FCSTD DOCUMENT  (FreeCAD 0.20R29177 +426 (Git))
Label: ASM_ExtensionArm
License: All rights reserved
LicenseURL: http://en.wikipedia.org/wiki/All_rights_reserved
objects: App::Link×7, App::DocumentObjectGroup×4, PartDesign::CoordinateSystem×3, App::FeaturePython×1, Part::FeaturePython×1, App::Part×1
note: 4 computed .brp shape members not serialized (recipe doc carries the construction recipe); baked Part::Feature solids carry a one-line shape summary decoded from their .brp
EXTERNAL_REF file=ASM_GantrySkate.FCStd obj=LCS_Origin
EXTERNAL_REF file=Params.FCStd obj=Spreadsheet
EXTERNAL_REF file=ASM_GantrySkate.FCStd obj=Assembly
EXTERNAL_REF file=../../../../../../AppData/Local/Temp/FreeCAD/Cache/FreeCAD_Doc_665ddbc1-c403-4c85-9c79-733a05948db3_da39a3_5468 obj=Assembly
EXTERNAL_REF file=AlExtrusion2040.FCStd obj=Assembly
EXTERNAL_REF file=ASM_ExtensionDriver.FCStd obj=LCS_Origin
EXTERNAL_REF file=ASM_ExtensionDriver.FCStd obj=Assembly
EXTERNAL_REF file=EndStopRear.FCStd obj=LCS_Origin
EXTERNAL_REF file=EndStopRear.FCStd obj=Assembly
EXTERNAL_REF file=BeltRetainerRear.FCStd obj=LCS_Origin
EXTERNAL_REF file=BeltRetainerRear.FCStd obj=Assembly
EXTERNAL_REF file=ASM_ExtensionHead.FCStd obj=LCS_Origin
EXTERNAL_REF file=ASM_ExtensionHead.FCStd obj=Assembly

FEATURE [App::DocumentObjectGroup] Parts
FEATURE [PartDesign::CoordinateSystem] LCS_Origin
  AttacherType = Attacher::AttachEngine3D
  MapMode = 2
  Support = -> [X_Axis]
FEATURE [App::FeaturePython] Variables  # WARN: FeaturePython — macro-defined, semantics opaque (R4)
  Retraction = 300
  Type = App::PropertyContainer
FEATURE [App::DocumentObjectGroup] Constraints
FEATURE [App::DocumentObjectGroup] Configurations
FEATURE [App::Link] ASM_GantrySkate  label="ASM_GantrySkate001"
  AttachedBy = #LCS_Origin
  AttachedTo = Parent Assembly#LCS_Origin
  AttachmentOffset = pos=(0,-150,0) rot=(0,1,0;3.14159rad)
  LinkPlacement = pos=(0,-150,0) rot=(0,1,0;3.14159rad)
  LinkedObject = -> <external ASM_GantrySkate.FCStd>#Assembly
  Placement = pos=(0,-150,0) rot=(0,1,0;3.14159rad)
  SolverId = Asm4EE
  expr: .AttachmentOffset.Base.y = <<Params>>#<<Params>>.RearSkateOffset * -1
  expr: Placement = LCS_Origin.Placement * AttachmentOffset * ASM_GantrySkate#LCS_Origin.Placement ^ -1
FEATURE [App::Link] ASM_GantrySkate001  label="ASM_GantrySkate002"
  AttachedBy = #LCS_Origin
  AttachedTo = Parent Assembly#LCS_Origin
  AttachmentOffset = pos=(0,350,0) rot=(0,1,0;3.14159rad)
  LinkPlacement = pos=(0,350,0) rot=(0,1,0;3.14159rad)
  LinkedObject = -> <external ASM_GantrySkate.FCStd>#Assembly
  Placement = pos=(0,350,0) rot=(0,1,0;3.14159rad)
  SolverId = Asm4EE
  expr: .AttachmentOffset.Base.y = <<Params>>#<<Params>>.FrontSkateOffset
  expr: Placement = LCS_Origin.Placement * AttachmentOffset * ASM_GantrySkate#LCS_Origin.Placement ^ -1
FEATURE [Part::FeaturePython] AlExtrusion2040_var  # link proxy (typed FeaturePython)
  AttachedBy = #LCS_Origin
  AttachedTo = Parent Assembly#LCS_EndStop
  AttachmentOffset = pos=(0,0,0) rot=(0.57735,-0.57735,-0.57735;4.18879rad)
  Length = 2000
  LinkedObject = -> <external ../../../../../../AppData/Local/Temp/FreeCAD/Cache/FreeCAD_Doc_665ddbc1-c403-4c85-9c79-733a05948db3_da39a3_5468>#Assembly
  Placement = pos=(2.9e-15,-482,-23.5) rot=(-0.57735,-0.57735,-0.57735;2.0944rad)
  SolverId = Asm4EE
  SourceObject = -> <external AlExtrusion2040.FCStd>#Assembly
  expr: Placement = LCS_EndStop.Placement * AttachmentOffset * varTmpDoc_3#LCS_Origin.Placement ^ -1
FEATURE [App::Link] ASM_ExtensionDriver
  AttachedBy = #LCS_Origin
  AttachedTo = Parent Assembly#LCS_Origin
  AttachmentOffset = pos=(-36,100,0) rot=(0.707107,0.707107,0;3.14159rad)
  LinkPlacement = pos=(-36,100,0) rot=(0.707107,0.707107,0;3.14159rad)
  LinkedObject = -> <external ASM_ExtensionDriver.FCStd>#Assembly
  Placement = pos=(-36,100,0) rot=(0.707107,0.707107,0;3.14159rad)
  SolverId = Asm4EE
  expr: Placement = LCS_Origin.Placement * AttachmentOffset * ASM_ExtensionDriver#LCS_Origin.Placement ^ -1
FEATURE [App::DocumentObjectGroup] Fasteners
FEATURE [App::Link] EndStopRear
  AttachedBy = #LCS_Origin
  AttachedTo = Parent Assembly#LCS_EndStop
  AttachmentOffset = pos=(0,0,0) rot=(1,0,0;1.5708rad)
  LinkPlacement = pos=(2.9e-15,-482,-23.5) rot=(0,0.707107,-0.707107;3.14159rad)
  LinkedObject = -> <external EndStopRear.FCStd>#Assembly
  Placement = pos=(2.9e-15,-482,-23.5) rot=(0,0.707107,-0.707107;3.14159rad)
  SolverId = Asm4EE
  expr: Placement = LCS_EndStop.Placement * AttachmentOffset * EndStopRear#LCS_Origin.Placement ^ -1
FEATURE [PartDesign::CoordinateSystem] ASM_GantrySkate_LCS_Origin
  AttachedBy = Origin
  AttacherType = Attacher::AttachEngine3D
  Placement = pos=(0,-150,0) rot=(0,1,0;3.14159rad)
  SolverId = Asm4EE
  expr: Placement = ASM_GantrySkate.Placement * ASM_GantrySkate#LCS_Origin.Placement
FEATURE [PartDesign::CoordinateSystem] LCS_EndStop
  AttacherType = Attacher::AttachEngine3D
  AttachmentOffset = pos=(0,-332,23.5) rot=(0,0,1;0rad)
  MapMode = 2
  Placement = pos=(2.9e-15,-482,-23.5) rot=(0,1,0;3.14159rad)
  Support = -> [ASM_GantrySkate_LCS_Origin]
  expr: .AttachmentOffset.Base.y = -32 - <<Variables>>.Retraction
FEATURE [App::Link] BeltRetainerRear
  AttachedBy = #LCS_Origin
  AttachedTo = Parent Assembly#LCS_EndStop
  AttachmentOffset = pos=(10,30,10) rot=(0.57735,0.57735,0.57735;2.0944rad)
  LinkPlacement = pos=(-10,-452,-33.5) rot=(0.57735,0.57735,-0.57735;4.18879rad)
  LinkedObject = -> <external BeltRetainerRear.FCStd>#Assembly
  Placement = pos=(-10,-452,-33.5) rot=(0.57735,0.57735,-0.57735;4.18879rad)
  SolverId = Asm4EE
  expr: Placement = LCS_EndStop.Placement * AttachmentOffset * BeltRetainerRear#LCS_Origin.Placement ^ -1
FEATURE [App::Link] BeltRetainerRear001  label="BeltRetainerTip"
  AttachedBy = #LCS_Origin
  AttachedTo = Parent Assembly#LCS_EndStop
  AttachmentOffset = pos=(10,1977,10) rot=(0.57735,-0.57735,0.57735;4.18879rad)
  LinkPlacement = pos=(-10,1495,-33.5) rot=(0.57735,-0.57735,-0.57735;2.0944rad)
  LinkedObject = -> <external BeltRetainerRear.FCStd>#Assembly
  Placement = pos=(-10,1495,-33.5) rot=(0.57735,-0.57735,-0.57735;2.0944rad)
  SolverId = Asm4EE
  expr: Placement = LCS_EndStop.Placement * AttachmentOffset * BeltRetainerRear#LCS_Origin.Placement ^ -1
FEATURE [App::Link] ASM_ExtensionHead
  AttachedBy = #LCS_Origin
  AttachedTo = Parent Assembly#LCS_EndStop
  AttachmentOffset = pos=(0,2000,0) rot=(0,1,0;3.14159rad)
  LinkPlacement = pos=(2.9e-15,1518,-23.5) rot=(0,0,1;0rad)
  LinkedObject = -> <external ASM_ExtensionHead.FCStd>#Assembly
  Placement = pos=(2.9e-15,1518,-23.5) rot=(0,0,1;0rad)
  SolverId = Asm4EE
  expr: .AttachmentOffset.Base.y = <<AlExtrusion2040_var>>.Length
  expr: Placement = LCS_EndStop.Placement * AttachmentOffset * ASM_ExtensionHead#LCS_Origin.Placement ^ -1
FEATURE [App::Part] Assembly
  AssemblyType = Part::Link
  Group = -> [LCS_Origin,Variables,Constraints,Configurations,ASM_GantrySkate,ASM_GantrySkate001,AlExtrusion2040_var,ASM_ExtensionDriver,Fasteners,EndStopRear,LCS_EndStop,ASM_GantrySkate_LCS_Origin,BeltRetainerRear,BeltRetainerRear001,ASM_ExtensionHead]
  Origin = -> Origin
  Type = Assembly

RESOLVED EXTERNAL PARTS (link-assembly join: the EXTERNAL_REF files above that resolve inside this repo's crawl, each included once):
---- part ASM_ExtensionDriver.FCStd = doc fcstd_9ed249eb061f ----
FCSTD DOCUMENT  (FreeCAD 0.20R29177 +426 (Git))
Label: ASM_ExtensionDriver
License: All rights reserved
LicenseURL: http://en.wikipedia.org/wiki/All_rights_reserved
objects: App::Link×5, App::DocumentObjectGroup×3, PartDesign::CoordinateSystem×1, App::FeaturePython×1, App::Part×1
note: 1 computed .brp shape members not serialized (recipe doc carries the construction recipe); baked Part::Feature solids carry a one-line shape summary decoded from their .brp
EXTERNAL_REF file=ASM_Stepper.FCStd obj=LCS_Origin
EXTERNAL_REF file=ASM_Stepper.FCStd obj=Assembly
EXTERNAL_REF file=ASM_Stepper.FCStd obj=Stepper_LCS_mount
EXTERNAL_REF file=SerpentinePlate.FCStd obj=LCS_Origin
EXTERNAL_REF file=SerpentinePlate.FCStd obj=Assembly
EXTERNAL_REF file=TimingPulleyGT2.FCStd obj=LCS_Origin
EXTERNAL_REF file=TimingPulleyGT2.FCStd obj=Assembly
EXTERNAL_REF file=SerpentinePlate.FCStd obj=LCS_idler1
EXTERNAL_REF file=SmoothIdlerPulleyGT2.FCStd obj=LCS_Origin
EXTERNAL_REF file=SmoothIdlerPulleyGT2.FCStd obj=Assembly
EXTERNAL_REF file=SerpentinePlate.FCStd obj=LCS_idler2

FEATURE [App::DocumentObjectGroup] Parts
FEATURE [PartDesign::CoordinateSystem] LCS_Origin
  AttacherType = Attacher::AttachEngine3D
  MapMode = 2
  Support = -> [X_Axis]
FEATURE [App::FeaturePython] Variables  # WARN: FeaturePython — macro-defined, semantics opaque (R4)
  Type = App::PropertyContainer
FEATURE [App::DocumentObjectGroup] Constraints
FEATURE [App::DocumentObjectGroup] Configurations
FEATURE [App::Link] ASM_Stepper
  AttachedBy = #LCS_Origin
  AttachedTo = Parent Assembly#LCS_Origin
  LinkedObject = -> <external ASM_Stepper.FCStd>#Assembly
  SolverId = Asm4EE
  expr: Placement = LCS_Origin.Placement * AttachmentOffset * ASM_Stepper#LCS_Origin.Placement ^ -1
FEATURE [App::Link] SerpentinePlate
  AttachedBy = #LCS_Origin
  AttachedTo = ASM_Stepper#Stepper_LCS_mount
  AttachmentOffset = pos=(0,0,-3) rot=(-1,0,0;3.14159rad)
  LinkPlacement = pos=(0,-7.1e-15,30) rot=(-1,0,0;1.5708rad)
  LinkedObject = -> <external SerpentinePlate.FCStd>#Assembly
  Placement = pos=(0,-7.1e-15,30) rot=(-1,0,0;1.5708rad)
  SolverId = Asm4EE
  expr: Placement = ASM_Stepper.Placement * ASM_Stepper#Stepper_LCS_mount.Placement * AttachmentOffset * SerpentinePlate#LCS_Origin.Placement ^ -1
FEATURE [App::Link] TimingPulleyGT2
  AttachedBy = #LCS_Origin
  AttachedTo = ASM_Stepper#Stepper_LCS_mount
  AttachmentOffset = pos=(0,0,-26) rot=(0,0,1;0rad)
  LinkPlacement = pos=(0,23,30) rot=(1,0,0;1.5708rad)
  LinkedObject = -> <external TimingPulleyGT2.FCStd>#Assembly
  Placement = pos=(0,23,30) rot=(1,0,0;1.5708rad)
  SolverId = Asm4EE
  expr: Placement = ASM_Stepper.Placement * ASM_Stepper#Stepper_LCS_mount.Placement * AttachmentOffset * TimingPulleyGT2#LCS_Origin.Placement ^ -1
FEATURE [App::Link] SmoothIdlerPulleyGT2
  AttachedBy = #LCS_Origin
  AttachedTo = SerpentinePlate#LCS_idler1
  AttachmentOffset = pos=(0,0,1) rot=(0,0,1;0rad)
  LinkPlacement = pos=(16.3,8,37.5) rot=(-1,0,0;1.5708rad)
  LinkedObject = -> <external SmoothIdlerPulleyGT2.FCStd>#Assembly
  Placement = pos=(16.3,8,37.5) rot=(-1,0,0;1.5708rad)
  SolverId = Asm4EE
  expr: Placement = SerpentinePlate.Placement * SerpentinePlate#LCS_idler1.Placement * AttachmentOffset * SmoothIdlerPulleyGT2#LCS_Origin.Placement ^ -1
FEATURE [App::Link] SmoothIdlerPulleyGT003
  AttachedBy = #LCS_Origin
  AttachedTo = SerpentinePlate#LCS_idler2
  AttachmentOffset = pos=(0,0,1) rot=(0,0,1;0rad)
  LinkPlacement = pos=(-16.3,8,37.5) rot=(-1,0,0;1.5708rad)
  LinkedObject = -> <external SmoothIdlerPulleyGT2.FCStd>#Assembly
  Placement = pos=(-16.3,8,37.5) rot=(-1,0,0;1.5708rad)
  SolverId = Asm4EE
  expr: Placement = SerpentinePlate.Placement * SerpentinePlate#LCS_idler2.Placement * AttachmentOffset * SmoothIdlerPulleyGT2#LCS_Origin.Placement ^ -1
FEATURE [App::Part] Assembly
  AssemblyType = Part::Link
  Group = -> [LCS_Origin,Variables,Constraints,Configurations,ASM_Stepper,SerpentinePlate,TimingPulleyGT2,SmoothIdlerPulleyGT2,SmoothIdlerPulleyGT003]
  Origin = -> Origin
  Type = Assembly
---- part ASM_ExtensionHead.FCStd = doc fcstd_2c640205720b ----
FCSTD DOCUMENT  (FreeCAD 0.20R29177 +426 (Git))
Label: ASM_ExtensionHead
License: All rights reserved
LicenseURL: http://en.wikipedia.org/wiki/All_rights_reserved
objects: App::Link×6, App::DocumentObjectGroup×3, PartDesign::CoordinateSystem×1, App::FeaturePython×1, App::Part×1
note: 1 computed .brp shape members not serialized (recipe doc carries the construction recipe); baked Part::Feature solids carry a one-line shape summary decoded from their .brp
EXTERNAL_REF file=EndStopTip.FCStd obj=LCS_Origin
EXTERNAL_REF file=EndStopTip.FCStd obj=Assembly
EXTERNAL_REF file=BreakawayMagnet.FCStd obj=LCS_Origin
EXTERNAL_REF file=EndStopTip.FCStd obj=Variables
EXTERNAL_REF file=BreakawayMagnet.FCStd obj=Assembly
EXTERNAL_REF file=BreakawayHeadBase.FCStd obj=LCS_Origin
EXTERNAL_REF file=EndStopTip.FCStd obj=Pad
EXTERNAL_REF file=EndStopTip.FCStd obj=Pad001
EXTERNAL_REF file=BreakawayHeadBase.FCStd obj=Assembly
EXTERNAL_REF file=ASM_TrussPulley.FCStd obj=LCS_Origin
EXTERNAL_REF file=BreakawayHeadBase.FCStd obj=Sketch002
EXTERNAL_REF file=BreakawayHeadTruss.FCStd obj=Variables
EXTERNAL_REF file=ASM_TrussPulley.FCStd obj=Assembly
EXTERNAL_REF file=HeadTetherMountClip.FCStd obj=LCS_Origin
EXTERNAL_REF file=HeadTetherMountClip.FCStd obj=Assembly

FEATURE [App::DocumentObjectGroup] Parts
FEATURE [PartDesign::CoordinateSystem] LCS_Origin
  AttacherType = Attacher::AttachEngine3D
  MapMode = 2
  Support = -> [X_Axis]
FEATURE [App::FeaturePython] Variables  # WARN: FeaturePython — macro-defined, semantics opaque (R4)
  Type = App::PropertyContainer
FEATURE [App::DocumentObjectGroup] Constraints
FEATURE [App::DocumentObjectGroup] Configurations
FEATURE [App::Link] EndStopTip
  AttachedBy = #LCS_Origin
  AttachedTo = Parent Assembly#LCS_Origin
  AttachmentOffset = pos=(0,0,0) rot=(0,-0.707107,-0.707107;3.14159rad)
  LinkPlacement = pos=(0,0,0) rot=(0,-0.707107,-0.707107;3.14159rad)
  LinkedObject = -> <external EndStopTip.FCStd>#Assembly
  Placement = pos=(0,0,0) rot=(0,-0.707107,-0.707107;3.14159rad)
  SolverId = Asm4EE
  expr: Placement = LCS_Origin.Placement * AttachmentOffset * EndStopTip#LCS_Origin.Placement ^ -1
FEATURE [App::Link] BreakawayMagnet  label="BreakawayMagnetTop"
  AttachedBy = #LCS_Origin
  AttachedTo = EndStopTip#LCS_Origin
  AttachmentOffset = pos=(0,-10,5) rot=(0,0,1;0rad)
  LinkPlacement = pos=(-1.3e-15,5,-10) rot=(0,-0.707107,-0.707107;3.14159rad)
  LinkedObject = -> <external BreakawayMagnet.FCStd>#Assembly
  Placement = pos=(-1.3e-15,5,-10) rot=(0,-0.707107,-0.707107;3.14159rad)
  SolverId = Asm4EE
  expr: .AttachmentOffset.Base.z = <<EndStopTip>>#<<Variables>>.BaseHeight
  expr: Placement = EndStopTip.Placement * EndStopTip#LCS_Origin.Placement * AttachmentOffset * BreakawayMagnet#LCS_Origin.Placement ^ -1
FEATURE [App::Link] BreakawayMagnet001  label="BreakawayMagnetBottom"
  AttachedBy = #LCS_Origin
  AttachedTo = EndStopTip#LCS_Origin
  AttachmentOffset = pos=(0,10,5) rot=(0,0,1;0rad)
  LinkPlacement = pos=(4e-16,5,10) rot=(0,-0.707107,-0.707107;3.14159rad)
  LinkedObject = -> <external BreakawayMagnet.FCStd>#Assembly
  Placement = pos=(4e-16,5,10) rot=(0,-0.707107,-0.707107;3.14159rad)
  SolverId = Asm4EE
  expr: .AttachmentOffset.Base.z = <<EndStopTip>>#<<Variables>>.BaseHeight
  expr: Placement = EndStopTip.Placement * EndStopTip#LCS_Origin.Placement * AttachmentOffset * BreakawayMagnet#LCS_Origin.Placement ^ -1
FEATURE [App::Link] BreakawayHeadBase
  AttachedBy = #LCS_Origin
  AttachedTo = EndStopTip#LCS_Origin
  AttachmentOffset = pos=(0,0,10) rot=(0,-0.707107,0.707107;3.14159rad)
  LinkPlacement = pos=(-9e-16,10,-2.2e-15) rot=(-1,0,0;3.14159rad)
  LinkedObject = -> <external BreakawayHeadBase.FCStd>#Assembly
  Placement = pos=(-9e-16,10,-2.2e-15) rot=(-1,0,0;3.14159rad)
  SolverId = Asm4EE
  expr: .AttachmentOffset.Base.z = <<EndStopTip>>#<<Pad>>.Length + <<EndStopTip>>#<<MagnetPad>>.Length
  expr: Placement = EndStopTip.Placement * EndStopTip#LCS_Origin.Placement * AttachmentOffset * BreakawayHeadBase#LCS_Origin.Placement ^ -1
FEATURE [App::Link] ASM_TrussPulley
  AttachedBy = #LCS_Origin
  AttachedTo = BreakawayHeadBase#LCS_Origin
  AttachmentOffset = pos=(0,-18,-16) rot=(1,0,0;3.40339rad)
  LinkPlacement = pos=(-4e-15,28,16) rot=(1,0,0;0.261799rad)
  LinkedObject = -> <external ASM_TrussPulley.FCStd>#Assembly
  Placement = pos=(-4e-15,28,16) rot=(1,0,0;0.261799rad)
  SolverId = Asm4EE
  expr: .AttachmentOffset.Base.y = <<BreakawayHeadBase>>#<<Sketch002>>.Constraints.HolesOffset * -1
  expr: .AttachmentOffset.Base.z = <<BreakawayHeadBase>>#<<Sketch002>>.Constraints.TrussHoleSpacing / -2
  expr: .AttachmentOffset.Rotation.Angle = 180 + <<BreakawayHeadTruss>>#<<Variables>>.TrussAngle
  expr: Placement = BreakawayHeadBase.Placement * BreakawayHeadBase#LCS_Origin.Placement * AttachmentOffset * ASM_TrussPulley#LCS_Origin.Placement ^ -1
FEATURE [App::Link] HeadTetherMountClip
  AttachedBy = #LCS_Origin
  AttachedTo = Parent Assembly#LCS_Origin
  AttachmentOffset = pos=(10,-18,-10) rot=(0.57735,0.57735,0.57735;2.0944rad)
  LinkPlacement = pos=(10,-18,-10) rot=(0.57735,0.57735,0.57735;2.0944rad)
  LinkedObject = -> <external HeadTetherMountClip.FCStd>#Assembly
  Placement = pos=(10,-18,-10) rot=(0.57735,0.57735,0.57735;2.0944rad)
  SolverId = Asm4EE
  expr: Placement = LCS_Origin.Placement * AttachmentOffset * HeadTetherMountClip#LCS_Origin.Placement ^ -1
FEATURE [App::Part] Assembly
  AssemblyType = Part::Link
  Group = -> [LCS_Origin,Variables,Constraints,Configurations,EndStopTip,BreakawayMagnet,BreakawayMagnet001,BreakawayHeadBase,ASM_TrussPulley,HeadTetherMountClip]
  Origin = -> Origin
  Type = Assembly
---- part ASM_GantrySkate.FCStd = doc fcstd_b04221d5cb82 ----
FCSTD DOCUMENT  (FreeCAD 0.20R29177 +426 (Git))
Label: ASM_GantrySkate
License: All rights reserved
LicenseURL: http://en.wikipedia.org/wiki/All_rights_reserved
objects: Part::FeaturePython×6, App::Link×5, App::DocumentObjectGroup×4, PartDesign::CoordinateSystem×1, App::FeaturePython×1, App::Part×1
note: 7 computed .brp shape members not serialized (recipe doc carries the construction recipe); baked Part::Feature solids carry a one-line shape summary decoded from their .brp
EXTERNAL_REF file=GantryBracket.FCStd obj=LCS_Origin
EXTERNAL_REF file=GantryBracket.FCStd obj=Assembly
EXTERNAL_REF file=GantryBracket.FCStd obj=LCS_wheel1
EXTERNAL_REF file=GantryWheel.FCStd obj=LCS_Origin
EXTERNAL_REF file=GantryWheel.FCStd obj=Assembly
EXTERNAL_REF file=GantryBracket.FCStd obj=LCS_wheel2
EXTERNAL_REF file=GantryBracket.FCStd obj=LCS_wheel3
EXTERNAL_REF file=GantryBracket.FCStd obj=LCS_wheel4
EXTERNAL_REF file=Params.FCStd obj=Spreadsheet
EXTERNAL_REF file=GantryBracket.FCStd obj=Sketch
EXTERNAL_REF file=GantryBracket.FCStd obj=Pad

FEATURE [App::DocumentObjectGroup] Parts
FEATURE [PartDesign::CoordinateSystem] LCS_Origin
  AttacherType = Attacher::AttachEngine3D
  MapMode = 2
  Support = -> [X_Axis]
FEATURE [App::FeaturePython] Variables  # WARN: FeaturePython — macro-defined, semantics opaque (R4)
  Type = App::PropertyContainer
FEATURE [App::DocumentObjectGroup] Constraints
FEATURE [App::DocumentObjectGroup] Configurations
FEATURE [App::Link] GantryBracket
  AttachedBy = #LCS_Origin
  AttachedTo = Parent Assembly#LCS_Origin
  LinkedObject = -> <external GantryBracket.FCStd>#Assembly
  SolverId = Asm4EE
  expr: Placement = LCS_Origin.Placement * AttachmentOffset * GantryBracket#LCS_Origin.Placement ^ -1
FEATURE [App::Link] GantryWheel
  AttachedBy = #LCS_Origin
  AttachedTo = GantryBracket#LCS_wheel1
  LinkPlacement = pos=(-19.85,20,3) rot=(0,0,1;1.5708rad)
  LinkedObject = -> <external GantryWheel.FCStd>#Assembly
  Placement = pos=(-19.85,20,3) rot=(0,0,1;1.5708rad)
  SolverId = Asm4EE
  expr: Placement = GantryBracket.Placement * GantryBracket#LCS_wheel1.Placement * AttachmentOffset * GantryWheel#LCS_Origin.Placement ^ -1
FEATURE [App::Link] GantryWheel001
  AttachedBy = #LCS_Origin
  AttachedTo = GantryBracket#LCS_wheel2
  LinkPlacement = pos=(19.85,20,3) rot=(0,0,1;1.5708rad)
  LinkedObject = -> <external GantryWheel.FCStd>#Assembly
  Placement = pos=(19.85,20,3) rot=(0,0,1;1.5708rad)
  SolverId = Asm4EE
  expr: Placement = GantryBracket.Placement * GantryBracket#LCS_wheel2.Placement * AttachmentOffset * GantryWheel#LCS_Origin.Placement ^ -1
FEATURE [App::Link] GantryWheel002
  AttachedBy = #LCS_Origin
  AttachedTo = GantryBracket#LCS_wheel3
  LinkPlacement = pos=(-19.85,-20,3) rot=(0,0,1;1.5708rad)
  LinkedObject = -> <external GantryWheel.FCStd>#Assembly
  Placement = pos=(-19.85,-20,3) rot=(0,0,1;1.5708rad)
  SolverId = Asm4EE
  expr: Placement = GantryBracket.Placement * GantryBracket#LCS_wheel3.Placement * AttachmentOffset * GantryWheel#LCS_Origin.Placement ^ -1
FEATURE [App::Link] GantryWheel003
  AttachedBy = #LCS_Origin
  AttachedTo = GantryBracket#LCS_wheel4
  LinkPlacement = pos=(19.85,-20,3) rot=(0,0,1;1.5708rad)
  LinkedObject = -> <external GantryWheel.FCStd>#Assembly
  Placement = pos=(19.85,-20,3) rot=(0,0,1;1.5708rad)
  SolverId = Asm4EE
  expr: Placement = GantryBracket.Placement * GantryBracket#LCS_wheel4.Placement * AttachmentOffset * GantryWheel#LCS_Origin.Placement ^ -1
FEATURE [Part::FeaturePython] Screw  label="M5x16-Screw"  # Fasteners workbench fastener (typed FeaturePython)
  Placement = pos=(19.85,0,-3.156) rot=(1,0,0;3.14159rad)
  baseObject = -> <external GantryBracket.FCStd>#Sketch [Edge23]
  diameter = 5
  invert = true
  leftHanded = false
  length = 3
  lengthCustom = 16
  matchOuter = false
  offset = 3.156
  thread = false
  type = 18
  expr: offset = <<Params>>#<<Params>>.SheetMetalThickness * 1mm + 0.5mm
FEATURE [Part::FeaturePython] Washer  label="M5-Washer"  # Fasteners workbench fastener (typed FeaturePython)
  Placement = pos=(19.85,0,3) rot=(0,0,1;0rad)
  baseObject = -> <external GantryBracket.FCStd>#Sketch [Edge23]
  diameter = 6
  invert = false
  matchOuter = false
  offset = 3
  type = 3
  expr: offset = <<GantryBracket>>#<<Pad>>.Length
FEATURE [Part::FeaturePython] Nut  label="M5-Nut"  # Fasteners workbench fastener (typed FeaturePython)
  Placement = pos=(19.85,0,4.1) rot=(0,0,1;0rad)
  baseObject = -> Washer [Edge1]
  diameter = 7
  invert = false
  leftHanded = false
  matchOuter = false
  offset = 0
  thread = false
  type = 7
FEATURE [Part::FeaturePython] Array_Screw  label="Array_M5x12-Screw"  # Draft array (typed FeaturePython)
  ArraySteps = 0
  ArrayType = Circular Array
  Axis = LCS_Origin.Z
  Count = 2
  ElementCount = 2
  FullAngle = 360
  IntervalAngle = 180
  LinearSteps = 0
  PlacementList = 2 placements: [(19.85,0,-3.156),(-19.85,2.43092e-15,-3.156)]
  ScaleList = (2) [(1,1,1),(1,1,1)]
  ShowElement = false
  SourceObject = -> Screw
FEATURE [Part::FeaturePython] Array_Washer  label="Array_M5-Washer"  # Draft array (typed FeaturePython)
  ArraySteps = 0
  ArrayType = Circular Array
  Axis = LCS_Origin.Z
  Count = 2
  ElementCount = 2
  FullAngle = 360
  IntervalAngle = 180
  LinearSteps = 0
  PlacementList = 2 placements: [(19.85,0,3),(-19.85,2.43092e-15,3)]
  ScaleList = (2) [(1,1,1),(1,1,1)]
  ShowElement = false
  SourceObject = -> Washer
FEATURE [Part::FeaturePython] Array_Nut  label="Array_M5-Nut"  # Draft array (typed FeaturePython)
  ArraySteps = 0
  ArrayType = Circular Array
  Axis = LCS_Origin.Z
  Count = 2
  ElementCount = 2
  FullAngle = 360
  IntervalAngle = 180
  LinearSteps = 0
  PlacementList = 2 placements: [(19.85,0,4.1),(-19.85,2.43092e-15,4.1)]
  ScaleList = (2) [(1,1,1),(1,1,1)]
  ShowElement = false
  SourceObject = -> Nut
FEATURE [App::DocumentObjectGroup] Fasteners
  Group = -> [Screw,Washer,Nut,Array_Screw,Array_Washer,Array_Nut]
FEATURE [App::Part] Assembly
  AssemblyType = Part::Link
  Group = -> [LCS_Origin,Variables,Constraints,Configurations,GantryBracket,GantryWheel,GantryWheel001,GantryWheel002,GantryWheel003,Fasteners,Screw,Array_Screw,Washer,Array_Washer,Nut,Array_Nut]
  Origin = -> Origin
  Type = Assembly
---- part AlExtrusion2040.FCStd = doc fcstd_94c1618523a2 ----
FCSTD DOCUMENT  (FreeCAD 0.20R29177 +426 (Git))
Label: AlExtrusion2040
License: All rights reserved
LicenseURL: http://en.wikipedia.org/wiki/All_rights_reserved
objects: App::DocumentObjectGroup×3, PartDesign::Mirrored×2, PartDesign::CoordinateSystem×1, App::FeaturePython×1, Sketcher::SketchObject×1, PartDesign::Pad×1, PartDesign::MultiTransform×1, PartDesign::Body×1, App::Part×1
note: 8 computed .brp shape members not serialized (recipe doc carries the construction recipe); baked Part::Feature solids carry a one-line shape summary decoded from their .brp

FEATURE [App::DocumentObjectGroup] Parts
FEATURE [PartDesign::CoordinateSystem] LCS_Origin
  AttacherType = Attacher::AttachEngine3D
  MapMode = 2
  Support = -> [X_Axis]
FEATURE [App::FeaturePython] Variables  # WARN: FeaturePython — macro-defined, semantics opaque (R4)
  Length = 100
  Type = App::PropertyContainer
FEATURE [App::DocumentObjectGroup] Constraints
FEATURE [App::DocumentObjectGroup] Configurations
FEATURE [Sketcher::SketchObject] Sketch
  FullyConstrained = true
  MapMode = 5
  Support = -> [XY_Plane001]
  sketch-geometry (30):
    g0: LineSegment StartX=0 StartY=10 StartZ=0 EndX=5.1 EndY=10 EndZ=0
    g1: LineSegment StartX=5.1 StartY=10 StartZ=0 EndX=6.9 EndY=8.2 EndZ=0
    g2: LineSegment StartX=6.9 StartY=8.2 StartZ=0 EndX=4.5 EndY=8.2 EndZ=0
    g3: LineSegment StartX=4.5 StartY=8.2 StartZ=0 EndX=4.5 EndY=6.56066 EndZ=0
    g4: LineSegment StartX=4.5 StartY=6.56066 StartZ=0 EndX=7.06066 EndY=4 EndZ=0
    g5: LineSegment StartX=7.06066 StartY=4 StartZ=0 EndX=12.9393 EndY=4 EndZ=0
    g6: LineSegment StartX=12.9393 StartY=4 StartZ=0 EndX=15.5 EndY=6.56066 EndZ=0
    g7: LineSegment StartX=15.5 StartY=6.56066 StartZ=0 EndX=15.5 EndY=8.2 EndZ=0
    g8: LineSegment StartX=15.5 StartY=8.2 StartZ=0 EndX=13.1 EndY=8.2 EndZ=0
    g9: LineSegment StartX=13.1 StartY=8.2 StartZ=0 EndX=14.9 EndY=10 EndZ=0
    g10: LineSegment StartX=14.9 StartY=10 StartZ=0 EndX=20 EndY=10 EndZ=0
    g11: LineSegment StartX=20 StartY=10 StartZ=0 EndX=20 EndY=4.9 EndZ=0
    g12: LineSegment StartX=20 StartY=4.9 StartZ=0 EndX=18.2 EndY=3.1 EndZ=0
    g13: LineSegment StartX=18.2 StartY=3.1 StartZ=0 EndX=18.2 EndY=5.5 EndZ=0
    g14: LineSegment StartX=18.2 StartY=5.5 StartZ=0 EndX=16.5607 EndY=5.5 EndZ=0
    g15: LineSegment StartX=16.5607 StartY=5.5 StartZ=0 EndX=14 EndY=2.93934 EndZ=0
    g16: LineSegment StartX=14 StartY=2.93934 StartZ=0 EndX=14 EndY=0 EndZ=0
    g17: LineSegment StartX=14 StartY=2.93934 StartZ=0 EndX=12.9393 EndY=4 EndZ=0
    g18: LineSegment StartX=14 StartY=0 StartZ=0 EndX=12.1 EndY=0 EndZ=0
    g19: ArcOfCircle CenterX=10 CenterY=0 CenterZ=0 NormalX=0 NormalY=0 NormalZ=1 AngleXU=0 Radius=2.1 StartAngle=0 EndAngle=3.14159
    g20: LineSegment StartX=7.9 StartY=3e-16 StartZ=0 EndX=6 EndY=3e-16 EndZ=0
    g21: LineSegment StartX=6 StartY=3e-16 StartZ=0 EndX=6 EndY=2.93934 EndZ=0
    g22: LineSegment StartX=6 StartY=2.93934 StartZ=0 EndX=3 EndY=5.93934 EndZ=0
    g23: LineSegment StartX=3 StartY=5.93934 StartZ=0 EndX=3 EndY=8.2 EndZ=0
    g24: LineSegment StartX=3 StartY=8.2 StartZ=0 EndX=0 EndY=8.2 EndZ=0
    g25: LineSegment StartX=0 StartY=10 StartZ=0 EndX=0 EndY=8.2 EndZ=0
    g26: LineSegment StartX=7.06066 StartY=4 StartZ=0 EndX=6 EndY=2.93934 EndZ=0
    g27: LineSegment StartX=3 StartY=8.2 StartZ=0 EndX=4.5 EndY=8.2 EndZ=0
    g28: GeomPoint X=10 Y=8.2 Z=0
    g29: LineSegment StartX=10 StartY=8.2 StartZ=0 EndX=10 EndY=0 EndZ=0
  constraints (85):
    c: PointOnObject(g0,g-2)
    c: Coincident(g0,g1)
    c: Coincident(g1,g2)
    c: Coincident(g2,g3)
    c: Coincident(g3,g4)
    c: Coincident(g4,g5)
    c: Horizontal(g5)
    c: Coincident(g5,g6)
    c: Coincident(g6,g7)
    c: Vertical(g7)
    c: Coincident(g7,g8)
    c: Horizontal(g8)
    c: Coincident(g8,g9)
    c: Coincident(g9,g10)
    c: Horizontal(g10)
    c: Coincident(g10,g11)
    c: Vertical(g11)
    c: Coincident(g11,g12)
    c: Coincident(g12,g13)
    c: Coincident(g13,g14)
    c: Coincident(g14,g15)
    c: Coincident(g15,g16)
    c: PointOnObject(g16,g-1)
    c: Vertical(g16)
    c: Horizontal(g14)
    c: Vertical(g13)
    c: Angle(g15,g-1) = 2.35619
    c: Parallel(g6,g15)
    c: Perpendicular(g6,g4)
    c: Vertical(g3)
    c: Horizontal(g2)
    c: Parallel(g1,g4)
    c: Horizontal(g0)
    c: Coincident(g17,g15)
    c: Coincident(g17,g5)
    c: Perpendicular(g15,g17)
    c: Distance(g17) = 1.5
    c: Coincident(g16,g18)
    c: PointOnObject(g18,g-1)
    c: PointOnObject(g19,g-1)
    c: Coincident(g19,g18)
    c: PointOnObject(g19,g-1)
    c: Coincident(g19,g20)
    c: Coincident(g20,g21)
    c: Vertical(g21)
    c: Coincident(g21,g22)
    c: Coincident(g22,g23)
    c: Vertical(g23)
    c: Coincident(g23,g24)
    c: PointOnObject(g24,g-2)
    c: Horizontal(g24)
    c: Coincident(g25,g0)
    c: Coincident(g25,g24)
    c: Parallel(g22,g4)
    c: Coincident(g26,g4)
    c: Coincident(g26,g21)
    c: Perpendicular(g22,g26)
    c: Equal(g26,g17)
    c: Equal(g7,g3)
    c: Coincident(g27,g23)
    c: Coincident(g27,g2)
    c: Horizontal(g27)
    c: DistanceY(g25,g25) = 1.8
    c: DistanceX(g-1,g19) = 10
    c: Horizontal(g20)
    c: Diameter(g19) = 4.2
    c: Equal(g27,g26)
    c: Parallel(g12,g15)
    c: Parallel(g9,g6)
    c: PointOnObject(g8,g2)
    c: PointOnObject(g9,g0)
    c: DistanceY(g-1,g0) = 10
    c: DistanceX(g2,g7) = 11
    c: DistanceX(g1,g8) = 6.2
    c: Equal(g14,g7)
    c: Equal(g13,g8)
    c: DistanceX(g0,g10) = 20
    c: Equal(g10,g11)
    c: Equal(g12,g9)
    c: Symmetric(g8,g1,g28)
    c: Coincident(g29,g28)
    c: Coincident(g29,g19)
    c: Vertical(g29)
    c: Equal(g18,g20)
    c: DistanceX(g20,g16) = 8
FEATURE [PartDesign::Pad] Pad
  Direction = (0,0,1)
  Length = 100
  Length2 = 10
  Profile = -> Sketch
  ReferenceAxis = -> Sketch [N_Axis]
  Type = 0
  expr: Length = <<Variables>>.Length
FEATURE [PartDesign::Mirrored] Mirrored
  MirrorPlane = -> Sketch [V_Axis]
FEATURE [PartDesign::Mirrored] Mirrored001
  MirrorPlane = -> Sketch [H_Axis]
FEATURE [PartDesign::MultiTransform] MultiTransform
  BaseFeature = -> Pad
  Originals = -> [Pad]
  Transformations = -> [Mirrored,Mirrored001]
FEATURE [PartDesign::Body] Body
  Group = -> [Sketch,Pad,MultiTransform,Mirrored,Mirrored001]
  Origin = -> Origin001
  Tip = -> MultiTransform
FEATURE [App::Part] Assembly
  AssemblyType = Part::Link
  Group = -> [LCS_Origin,Variables,Constraints,Configurations,Body]
  Origin = -> Origin
  Type = Assembly
---- part BeltRetainerRear.FCStd = doc fcstd_9e532c998300 ----
FCSTD DOCUMENT  (FreeCAD 0.20R29177 +426 (Git))
Label: BeltRetainerRear
License: All rights reserved
LicenseURL: http://en.wikipedia.org/wiki/All_rights_reserved
objects: Sketcher::SketchObject×7, Part::FeaturePython×6, App::DocumentObjectGroup×4, PartDesign::Pocket×3, PartDesign::Mirrored×3, PartDesign::CoordinateSystem×2, App::FeaturePython×1, PartDesign::Pad×1, PartDesign::Hole×1, PartDesign::SubtractivePipe×1, PartDesign::Line×1, PartDesign::PolarPattern×1, PartDesign::MultiTransform×1, PartDesign::Body×1, App::Part×1
note: 34 computed .brp shape members not serialized (recipe doc carries the construction recipe); baked Part::Feature solids carry a one-line shape summary decoded from their .brp

FEATURE [App::DocumentObjectGroup] Parts
FEATURE [PartDesign::CoordinateSystem] LCS_Origin
  AttacherType = Attacher::AttachEngine3D
  MapMode = 2
  Support = -> [X_Axis]
FEATURE [App::FeaturePython] Variables  # WARN: FeaturePython — macro-defined, semantics opaque (R4)
  BaseHeight = 4
  BeltCurveRadius = 10.5
  RibThickness = 2
  Type = App::PropertyContainer
FEATURE [App::DocumentObjectGroup] Constraints
FEATURE [App::DocumentObjectGroup] Configurations
FEATURE [Sketcher::SketchObject] Sketch
  FullyConstrained = true
  MapMode = 5
  Support = -> [XY_Plane001]
  sketch-geometry (10):
    g0: ArcOfCircle CenterX=-19 CenterY=5.5 CenterZ=0 NormalX=0 NormalY=0 NormalZ=1 AngleXU=0 Radius=3 StartAngle=1.5708 EndAngle=3.14159
    g1: ArcOfCircle CenterX=19 CenterY=5.5 CenterZ=0 NormalX=0 NormalY=0 NormalZ=1 AngleXU=0 Radius=3 StartAngle=0 EndAngle=1.5708
    g2: ArcOfCircle CenterX=19 CenterY=-5.5 CenterZ=0 NormalX=0 NormalY=0 NormalZ=1 AngleXU=0 Radius=3 StartAngle=4.71239 EndAngle=6.28319
    g3: LineSegment StartX=19 StartY=-8.5 StartZ=0 EndX=-19 EndY=-8.5 EndZ=0
    g4: ArcOfCircle CenterX=-19 CenterY=-5.5 CenterZ=0 NormalX=0 NormalY=0 NormalZ=1 AngleXU=0 Radius=3 StartAngle=3.14159 EndAngle=4.71239
    g5: LineSegment StartX=-22 StartY=-5.5 StartZ=0 EndX=-22 EndY=5.5 EndZ=0
    g6: GeomPoint X=-22 Y=8.5 Z=0
    g7: GeomPoint X=22 Y=-8.5 Z=0
    g8: LineSegment StartX=-19 StartY=8.5 StartZ=0 EndX=19 EndY=8.5 EndZ=0
    g9: LineSegment StartX=22 StartY=5.5 StartZ=0 EndX=22 EndY=-5.5 EndZ=0
  constraints (23):
    c: Tangent(g0,g8) = 1.5708
    c: Tangent(g9,g2) = 1.5708
    c: Tangent(g2,g3) = 1.5708
    c: Tangent(g3,g4) = 1.5708
    c: Tangent(g4,g5) = 1.5708
    c: Tangent(g5,g0) = 1.5708
    c: Horizontal(g3)
    c: Vertical(g5)
    c: Equal(g0,g1)
    c: Equal(g1,g2)
    c: Equal(g2,g4)
    c: PointOnObject(g6,g5)
    c: PointOnObject(g7,g3)
    c: Radius(g1) = 3
    c: DistanceX(g4,g9) = 44  'Width'
    c: Horizontal(g8)
    c: PointOnObject(g6,g8)
    c: Vertical(g9)
    c: PointOnObject(g7,g9)
    c: Tangent(g9,g1) = 1.5708
    c: Tangent(g8,g1) = 1.5708
    c: Symmetric(g2,g0,g-1)
    c: DistanceY(g3,g0) = 17  'Height'
FEATURE [PartDesign::Pad] Pad
  Direction = (0,0,1)
  Length = 17
  Length2 = 10
  Profile = -> Sketch
  ReferenceAxis = -> Sketch [N_Axis]
  Type = 0
FEATURE [Sketcher::SketchObject] Sketch001
  AttachmentOffset = pos=(0,0,4) rot=(0,0,1;0rad)
  FullyConstrained = true
  MapMode = 2
  Placement = pos=(0,0,4) rot=(0,0,1;0rad)
  Support = -> [XY_Plane]
  expr: .AttachmentOffset.Base.z = <<Variables>>.BaseHeight
  sketch-geometry (2):
    g0: Circle CenterX=-15 CenterY=0 CenterZ=0 NormalX=0 NormalY=0 NormalZ=1 AngleXU=0 Radius=1
    g1: Circle CenterX=15 CenterY=0 CenterZ=0 NormalX=0 NormalY=0 NormalZ=1 AngleXU=0 Radius=1
  constraints (5):
    c: PointOnObject(g0,g-1)
    c: Symmetric(g0,g1,g-1)
    c: Diameter(g1) = 2
    c: Equal(g1,g0)
    c: DistanceX(g0,g-1) = 15  'HoleOffset'
FEATURE [PartDesign::Hole] Hole  label="MountHoles"
  BaseFeature = -> Pad
  CustomThreadClearance = 0
  Depth = 25
  DepthType = 0
  Diameter = 5.5
  DrillForDepth = false
  DrillPoint = 1
  DrillPointAngle = 118
  HoleCutCountersinkAngle = 90
  HoleCutCustomValues = false
  HoleCutDepth = 0
  HoleCutDiameter = 6.1
  HoleCutType = 0
  ModelThread = false
  Profile = -> Sketch001
  Tapered = false
  TaperedAngle = 90
  ThreadClass = 0
  ThreadDepth = 25
  ThreadDepthType = 0
  ThreadDirection = 0
  ThreadFit = 0
  ThreadSize = 13
  ThreadType = 1
  Threaded = false
  UseCustomThreadClearance = false
FEATURE [Part::FeaturePython] Washer  label="M5-Washer"  # Fasteners workbench fastener (typed FeaturePython)
  Placement = pos=(-15,0,4) rot=(0,0,1;0rad)
  baseObject = -> Sketch001 [Edge1]
  diameter = 6
  invert = false
  matchOuter = false
  offset = 0
  type = 3
FEATURE [Part::FeaturePython] Screw  label="M5x10-Screw"  # Fasteners workbench fastener (typed FeaturePython)
  Placement = pos=(-15,0,5.1) rot=(0,0,1;0rad)
  baseObject = -> Washer [Edge1]
  diameter = 3
  invert = false
  leftHanded = false
  length = 1
  lengthCustom = 10
  matchOuter = false
  offset = 0
  thread = false
  type = 40
FEATURE [Part::FeaturePython] Array_Washer  label="Array_M5-Washer"  # Draft array (typed FeaturePython)
  ArraySteps = 0
  ArrayType = Circular Array
  Axis = LCS_Origin.Z
  Count = 2
  ElementCount = 2
  FullAngle = 360
  IntervalAngle = 180
  LinearSteps = 0
  PlacementList = 2 placements: [(-15,0,4),(15,-1.83697e-15,4)]
  ScaleList = (2) [(1,1,1),(1,1,1)]
  ShowElement = false
  SourceObject = -> Washer
FEATURE [Part::FeaturePython] Array_Screw  label="Array_M5x12-Screw"  # Draft array (typed FeaturePython)
  ArraySteps = 0
  ArrayType = Circular Array
  Axis = LCS_Origin.Z
  Count = 2
  ElementCount = 2
  FullAngle = 360
  IntervalAngle = 180
  LinearSteps = 0
  PlacementList = 2 placements: [(-15,0,5.1),(15,-1.83697e-15,5.1)]
  ScaleList = (2) [(1,1,1),(1,1,1)]
  ShowElement = false
  SourceObject = -> Screw
FEATURE [Sketcher::SketchObject] Sketch003
  AttachmentOffset = pos=(0,4,0) rot=(0,0,1;0rad)
  FullyConstrained = true
  MapMode = 5
  Placement = pos=(0,-9e-16,4) rot=(1,0,0;1.5708rad)
  Support = -> [XZ_Plane001]
  expr: .AttachmentOffset.Base.y = <<Variables>>.BaseHeight
  expr: Constraints[13] = <<Sketch001>>.Constraints.HoleOffset
  expr: Constraints[14] = <<Sketch>>.Constraints.Height / 2 - <<Variables>>.RibThickness * 1mm
  expr: Constraints[15] = <<Pad>>.Length
  sketch-geometry (9):
    g0: LineSegment StartX=-10 StartY=0 StartZ=0 EndX=-15 EndY=0 EndZ=0
    g1: LineSegment StartX=-15 StartY=0 StartZ=0 EndX=-15 EndY=17 EndZ=0
    g2: LineSegment StartX=-15 StartY=17 StartZ=0 EndX=-8.5 EndY=17 EndZ=0
    g3: LineSegment StartX=-8.5 StartY=17 StartZ=0 EndX=-8.5 EndY=1.5 EndZ=0
    g4: ArcOfCircle CenterX=-10 CenterY=1.5 CenterZ=0 NormalX=0 NormalY=0 NormalZ=1 AngleXU=0 Radius=1.5 StartAngle=4.71239 EndAngle=6.28319
    g5: GeomPoint X=-8.5 Y=0 Z=0
    g6: LineSegment StartX=-15 StartY=17 StartZ=0 EndX=-16 EndY=17 EndZ=0
    g7: LineSegment StartX=-16 StartY=17 StartZ=0 EndX=-16 EndY=0 EndZ=0
    g8: LineSegment StartX=-16 StartY=0 StartZ=0 EndX=-15 EndY=0 EndZ=0
  constraints (24):
    c: Coincident(g0,g1)
    c: Coincident(g1,g2)
    c: Coincident(g2,g3)
    c: Horizontal(g0)
    c: Horizontal(g2)
    c: Vertical(g1)
    c: Vertical(g3)
    c: PointOnObject(g5,g-1)
    c: PointOnObject(g5,g3)
    c: PointOnObject(g5,g0)
    c: Tangent(g3,g4) = 1.5708
    c: Tangent(g0,g4) = 1.5708
    c: Radius(g4) = 1.5
    c: DistanceX(g0,g-1) = 15
    c: DistanceX(g2,g2) = 6.5
    c: DistanceY(g1,g1) = 17
    c: Coincident(g2,g6)
    c: Horizontal(g6)
    c: Coincident(g6,g7)
    c: PointOnObject(g7,g-1)
    c: Vertical(g7)
    c: Coincident(g7,g8)
    c: Coincident(g8,g0)
    c: DistanceX(g8,g8) = 1
FEATURE [Sketcher::SketchObject] Sketch004
  AttachmentOffset = pos=(0,0,21) rot=(0,0,1;0rad)
  FullyConstrained = true
  MapMode = 5
  Placement = pos=(0,0,21) rot=(0,0,1;0rad)
  Support = -> [XY_Plane001]
  expr: .AttachmentOffset.Base.z = <<Variables>>.BaseHeight * 1mm + <<Sketch>>.Constraints.Height
  expr: Constraints[7] = <<Sketch001>>.Constraints.HoleOffset
  expr: Constraints[8] = <<Sketch>>.Constraints.Height - <<Variables>>.RibThickness * 2mm
  sketch-geometry (5):
    g0: ArcOfCircle CenterX=-15 CenterY=0 CenterZ=0 NormalX=0 NormalY=0 NormalZ=1 AngleXU=0 Radius=6.5 StartAngle=4.71239 EndAngle=7.85398
    g1: LineSegment StartX=-15 StartY=6.5 StartZ=0 EndX=-28 EndY=6.5 EndZ=0
    g2: LineSegment StartX=-28 StartY=-6.5 StartZ=0 EndX=-15 EndY=-6.5 EndZ=0
    g3: LineSegment StartX=-15 StartY=-6.5 StartZ=0 EndX=-15 EndY=6.5 EndZ=0
    g4: LineSegment StartX=-28 StartY=6.5 StartZ=0 EndX=-28 EndY=-6.5 EndZ=0
  constraints (13):
    c: PointOnObject(g0,g-1)
    c: Horizontal(g1)
    c: Horizontal(g2)
    c: Tangent(g1,g0) = -1.5708
    c: Tangent(g2,g0) = -1.5708
    c: Coincident(g0,g3)
    c: Coincident(g3,g0)
    c: DistanceX(g0,g-1) = 15
    c: DistanceY(g3,g3) = 13
    c: Equal(g3,g2)
    c: Coincident(g4,g1)
    c: Coincident(g4,g2)
    c: Vertical(g4)
FEATURE [PartDesign::CoordinateSystem] LCS_1  label="LCS_BeltCenter"
  AttacherType = Attacher::AttachEngine3D
  AttachmentOffset = pos=(7.5,0,17) rot=(0,0,1;0rad)
  MapMode = 2
  Placement = pos=(7.5,0,17) rot=(0,0,1;0rad)
  Support = -> [XY_Plane001]
  expr: .AttachmentOffset.Base.z = <<Pad>>.Length
FEATURE [Sketcher::SketchObject] Sketch002
  AttachmentOffset = pos=(-10.5,0,-6) rot=(0,0,1;0rad)
  FullyConstrained = true
  MapMode = 2
  Placement = pos=(-3,0,11) rot=(0,0,1;0rad)
  Support = -> [LCS_1]
  expr: .AttachmentOffset.Base.x = <<Variables>>.BeltCurveRadius * -1
  expr: Constraints[35] = <<Variables>>.BeltCurveRadius
  sketch-geometry (13):
    g0: ArcOfCircle CenterX=-0.0981633 CenterY=-1.3406 CenterZ=0 NormalX=0 NormalY=0 NormalZ=1 AngleXU=0 Radius=1.05 StartAngle=1.85527 EndAngle=2.42562
    g1: ArcOfCircle CenterX=-0.437669 CenterY=-1.04524 CenterZ=0 NormalX=0 NormalY=0 NormalZ=1 AngleXU=0 Radius=0.6 StartAngle=2.42562 EndAngle=3.23687
    g2: ArcOfCircle CenterX=-0.434948 CenterY=-0.188828 CenterZ=0 NormalX=0 NormalY=0 NormalZ=1 AngleXU=0 Radius=0.15 StartAngle=4.99686 EndAngle=6.28319
    g3: LineSegment StartX=-0.284948 StartY=-0.188828 StartZ=0 EndX=-0.284948 EndY=0 EndZ=0
    g4: LineSegment StartX=-0.437669 StartY=-1.04524 StartZ=0 EndX=0.657342 EndY=-0.940598 EndZ=0
    g5: ArcOfCircle CenterX=10.5 CenterY=0 CenterZ=0 NormalX=0 NormalY=0 NormalZ=1 AngleXU=0 Radius=9.8875 StartAngle=3.14159 EndAngle=3.23687
    g6: LineSegment StartX=0.657342 StartY=-0.940598 StartZ=0 EndX=0.567455 EndY=0 EndZ=0
    g7: LineSegment StartX=-0.284948 StartY=0 StartZ=0 EndX=0.612501 EndY=1.2e-15 EndZ=0
    g8: LineSegment StartX=-1.03495 StartY=-1.10232 StartZ=0 EndX=0.657342 EndY=-1.10232 EndZ=0
    g9: LineSegment StartX=0.657342 StartY=-1.10232 StartZ=0 EndX=0.657342 EndY=-0.940598 EndZ=0
    g10: ArcOfCircle CenterX=10.5 CenterY=0 CenterZ=0 NormalX=0 NormalY=0 NormalZ=1 AngleXU=0 Radius=11.5875 StartAngle=3.14159 EndAngle=3.23687
    g11: LineSegment StartX=-0.284948 StartY=-0.188828 StartZ=0 EndX=-0.205229 EndY=-1.02303 EndZ=0
    g12: ArcOfCircle CenterX=10.5 CenterY=0 CenterZ=0 NormalX=0 NormalY=0 NormalZ=1 AngleXU=0 Radius=10.5 StartAngle=3.14159 EndAngle=3.23687
  constraints (38):
    c: Radius(g0) = 1.05
    c: Tangent(g1,g0) = -1.5708
    c: Radius(g1) = 0.6
    c: Tangent(g2,g0) = 1.5708
    c: Radius(g2) = 0.15
    c: Tangent(g3,g2) = -1.5708
    c: Vertical(g3)
    c: Coincident(g4,g1)
    c: DistanceY(g0,g4) = 0.4
    c: PointOnObject(g1,g4)
    c: DistanceX(g1,g2) = 0.75
    c: PointOnObject(g5,g-1)
    c: Tangent(g6,g5) = 1.5708
    c: Coincident(g7,g3)
    c: Horizontal(g8)
    c: Coincident(g9,g8)
    c: Coincident(g9,g5)
    c: Vertical(g9)
    c: Distance(g5,g1) = 1.7
    c: Angle(g-1,g4) = 0.0952741  'HalfToothAngle'
    c: PointOnObject(g6,g7)
    c: PointOnObject(g3,g-1)
    c: Coincident(g5,g7)
    c: PointOnObject(g5,g-1)
    c: Coincident(g4,g5)
    c: Coincident(g10,g5)
    c: Coincident(g8,g1)
    c: Tangent(g10,g1) = -1.5708
    c: Coincident(g11,g2)
    c: PointOnObject(g11,g4)
    c: Perpendicular(g4,g11)
    c: Coincident(g12,g5)
    c: PointOnObject(g12,g4)
    c: Distance(g12,g11) = 0.254
    c: Coincident(g12,g-1)
    c: Radius(g12) = 10.5
    c: Distance(g12,g12) = 1
    c: PointOnObject(g10,g-1)
FEATURE [PartDesign::Pocket] Pocket  label="GT2_HalfTooth"
  BaseFeature = -> Hole
  Direction = (0,0,-1)
  Length = 5
  Length2 = 5
  Profile = -> Sketch002
  ReferenceAxis = -> Sketch002 [N_Axis]
  Reversed = true
  Type = 1
FEATURE [PartDesign::SubtractivePipe] SubtractivePipe  label="ScrewPocket"
  AuxilleryCurvelinear = true
  AuxillerySpineTangent = false
  BaseFeature = -> Pocket
  Binormal = (0,0,0)
  Mode = 0
  Profile = -> Sketch003
  Spine = -> Sketch004
  SpineTangent = false
  Transformation = 0
  Transition = 0
FEATURE [PartDesign::Mirrored] Mirrored
  MirrorPlane = -> Sketch002 [H_Axis]
FEATURE [PartDesign::Line] DatumLine
  AttacherType = Attacher::AttachEngineLine
  Length = 20
  MapMode = 18
  Placement = pos=(7.5,0,17) rot=(0,0,1;0rad)
  ResizeMode = 0
  Support = -> [LCS_1]
FEATURE [PartDesign::PolarPattern] PolarPattern
  Angle = 98.2585
  Axis = -> DatumLine
  Occurrences = 10
  expr: Angle = Sketch002.Constraints.HalfToothAngle * 2 * 9
FEATURE [PartDesign::Mirrored] Mirrored001
  MirrorPlane = -> Sketch002 [H_Axis]
FEATURE [PartDesign::MultiTransform] MultiTransform
  BaseFeature = -> SubtractivePipe
  Originals = -> [Pocket]
  Transformations = -> [Mirrored,PolarPattern,Mirrored001]
FEATURE [Sketcher::SketchObject] Sketch005
  FullyConstrained = true
  MapMode = 5
  Placement = pos=(0,0,0) rot=(1,0,0;1.5708rad)
  Support = -> [XZ_Plane001]
  expr: Constraints[7] = <<Pad>>.Length + 2mm
  expr: Constraints[8] = <<Sketch>>.Constraints.Width / 2 + 1mm
  sketch-geometry (3):
    g0: LineSegment StartX=-23 StartY=1 StartZ=0 EndX=-5 EndY=19 EndZ=0
    g1: LineSegment StartX=-5 StartY=19 StartZ=0 EndX=-23 EndY=19 EndZ=0
    g2: LineSegment StartX=-23 StartY=19 StartZ=0 EndX=-23 EndY=1 EndZ=0
  constraints (9):
    c: Coincident(g0,g1)
    c: Horizontal(g1)
    c: Coincident(g1,g2)
    c: Coincident(g2,g0)
    c: Vertical(g2)
    c: Equal(g1,g2)
    c: DistanceX(g1,g1) = 18
    c: DistanceY(g-1,g1) = 19
    c: DistanceX(g1,g-1) = 23
FEATURE [PartDesign::Pocket] Pocket001  label="Chamfer"
  BaseFeature = -> MultiTransform
  Direction = (0,1,2e-16)
  Length = 5
  Length2 = 5
  Midplane = true
  Profile = -> Sketch005
  ReferenceAxis = -> Sketch005 [N_Axis]
  Type = 1
FEATURE [PartDesign::Mirrored] Mirrored002  label="ScrewPocketMirror"
  BaseFeature = -> Pocket001
  MirrorPlane = -> Sketch003 [V_Axis]
  Originals = -> [SubtractivePipe,Pocket001]
FEATURE [Sketcher::SketchObject] Sketch006
  AttachmentOffset = pos=(0,0,17) rot=(0,0,1;0rad)
  FullyConstrained = true
  MapMode = 5
  Placement = pos=(0,0,17) rot=(0,0,1;0rad)
  Support = -> [XY_Plane001]
  expr: .AttachmentOffset.Base.z = <<Pad>>.Length
  sketch-geometry (1):
    g0: Circle CenterX=0 CenterY=0 CenterZ=0 NormalX=0 NormalY=0 NormalZ=1 AngleXU=0 Radius=1.85
  constraints (2):
    c: Diameter(g0) = 3.7
    c: Coincident(g0,g-1)
FEATURE [PartDesign::Pocket] Pocket002  label="BeltScrewHole"
  BaseFeature = -> Mirrored002
  Direction = (0,0,-1)
  Length = 10
  Length2 = 5
  Profile = -> Sketch006
  ReferenceAxis = -> Sketch006 [N_Axis]
  Type = 0
FEATURE [PartDesign::Body] Body
  Group = -> [Sketch,Pad,Sketch001,Hole,Sketch002,Pocket,Sketch003,Sketch004,SubtractivePipe,MultiTransform,Mirrored,PolarPattern,LCS_1,DatumLine,Mirrored001,Sketch005,Pocket001,Mirrored002,Sketch006,Pocket002]
  Origin = -> Origin001
  Tip = -> Pocket002
FEATURE [Part::FeaturePython] Washer001  label="M4-Washer"  # Fasteners workbench fastener (typed FeaturePython)
  Placement = pos=(0,0,17) rot=(0,0,1;0rad)
  diameter = 3
  invert = false
  matchOuter = false
  offset = 0
  type = 6
FEATURE [Part::FeaturePython] Screw001  label="M4x6-Screw"  # Fasteners workbench fastener (typed FeaturePython)
  Placement = pos=(0,0,18.1) rot=(0,0,1;0rad)
  diameter = 2
  invert = false
  leftHanded = false
  length = 0
  lengthCustom = 6
  matchOuter = false
  offset = 0
  thread = false
  type = 40
FEATURE [App::DocumentObjectGroup] Fasteners
  Group = -> [Washer,Screw,Array_Washer,Array_Screw,Washer001,Screw001]
FEATURE [App::Part] Assembly
  AssemblyType = Part::Link
  Group = -> [LCS_Origin,Variables,Constraints,Configurations,Body,Fasteners,Washer,Array_Washer,Screw,Array_Screw,Washer001,Screw001]
  Origin = -> Origin
  Type = Assembly
---- part EndStopRear.FCStd = doc fcstd_ffab53be4142 ----
FCSTD DOCUMENT  (FreeCAD 0.20R29177 +426 (Git))
Label: EndStopRear
License: All rights reserved
LicenseURL: http://en.wikipedia.org/wiki/All_rights_reserved
objects: Sketcher::SketchObject×5, App::DocumentObjectGroup×4, PartDesign::Pad×2, Part::FeaturePython×2, PartDesign::Pocket×2, PartDesign::CoordinateSystem×1, App::FeaturePython×1, PartDesign::Mirrored×1, PartDesign::Hole×1, PartDesign::Body×1, App::Part×1
note: 20 computed .brp shape members not serialized (recipe doc carries the construction recipe); baked Part::Feature solids carry a one-line shape summary decoded from their .brp

FEATURE [App::DocumentObjectGroup] Parts
FEATURE [PartDesign::CoordinateSystem] LCS_Origin
  AttacherType = Attacher::AttachEngine3D
  MapMode = 2
  Support = -> [X_Axis]
FEATURE [App::FeaturePython] Variables  # WARN: FeaturePython — macro-defined, semantics opaque (R4)
  Type = App::PropertyContainer
FEATURE [App::DocumentObjectGroup] Constraints
FEATURE [App::DocumentObjectGroup] Configurations
FEATURE [Sketcher::SketchObject] Sketch
  FullyConstrained = true
  MapMode = 5
  Support = -> [XY_Plane001]
  sketch-geometry (5):
    g0: LineSegment StartX=-22 StartY=-20 StartZ=0 EndX=-22 EndY=20 EndZ=0
    g1: LineSegment StartX=-22 StartY=20 StartZ=0 EndX=22 EndY=20 EndZ=0
    g2: LineSegment StartX=22 StartY=20 StartZ=0 EndX=22 EndY=-20 EndZ=0
    g3: LineSegment StartX=22 StartY=-20 StartZ=0 EndX=-22 EndY=-20 EndZ=0
    g4: GeomPoint X=0 Y=0 Z=0
  constraints (12):
    c: Coincident(g0,g1)
    c: Coincident(g1,g2)
    c: Coincident(g2,g3)
    c: Coincident(g3,g0)
    c: Horizontal(g1)
    c: Horizontal(g3)
    c: Vertical(g0)
    c: Vertical(g2)
    c: Symmetric(g1,g0,g4)
    c: Coincident(g4,g-1)
    c: DistanceY(g2,g2) = 40  'Height'
    c: DistanceX(g1,g1) = 44  'Width'
FEATURE [PartDesign::Pad] Pad
  Direction = (0,0,1)
  Length = 3
  Length2 = 10
  Profile = -> Sketch
  ReferenceAxis = -> Sketch [N_Axis]
  Type = 0
FEATURE [Sketcher::SketchObject] Sketch001
  AttachmentOffset = pos=(0,0,4) rot=(0,0,1;0rad)
  FullyConstrained = true
  MapMode = 5
  Placement = pos=(0,0,4) rot=(0,0,1;0rad)
  Support = -> [XY_Plane001]
  expr: .AttachmentOffset.Base.z = <<Pad>>.Length + 1mm
  sketch-geometry (2):
    g0: Circle CenterX=0 CenterY=10 CenterZ=0 NormalX=0 NormalY=0 NormalZ=1 AngleXU=0 Radius=1
    g1: Circle CenterX=0 CenterY=-10 CenterZ=0 NormalX=0 NormalY=0 NormalZ=1 AngleXU=0 Radius=1
  constraints (5):
    c: PointOnObject(g0,g-2)
    c: Equal(g0,g1)
    c: Diameter(g0) = 2
    c: Symmetric(g1,g0,g-1)
    c: DistanceY(g1,g0) = 20
FEATURE [Sketcher::SketchObject] Sketch002
  AttachmentOffset = pos=(0,3,0) rot=(0,0,1;0rad)
  FullyConstrained = true
  MapMode = 5
  Placement = pos=(0,-7e-16,3) rot=(1,0,0;1.5708rad)
  Support = -> [XZ_Plane001]
  expr: .AttachmentOffset.Base.y = <<Pad>>.Length
  expr: Constraints[9] = Sketch.Constraints.Width / 2
  sketch-geometry (4):
    g0: LineSegment StartX=0 StartY=10 StartZ=0 EndX=12 EndY=10 EndZ=0
    g1: LineSegment StartX=12 StartY=10 StartZ=0 EndX=22 EndY=0 EndZ=0
    g2: LineSegment StartX=22 StartY=0 StartZ=0 EndX=0 EndY=0 EndZ=0
    g3: LineSegment StartX=0 StartY=0 StartZ=0 EndX=0 EndY=10 EndZ=0
  constraints (11):
    c: PointOnObject(g0,g-2)
    c: Horizontal(g0)
    c: Coincident(g0,g1)
    c: PointOnObject(g1,g-1)
    c: Coincident(g1,g2)
    c: Coincident(g2,g-1)
    c: Coincident(g2,g3)
    c: Coincident(g3,g0)
    c: DistanceY(g3,g3) = 10
    c: DistanceX(g2,g2) = 22
    c: Angle(g1,g2) = 0.785398
FEATURE [PartDesign::Pad] Pad001  label="Rib"
  BaseFeature = -> Pad
  Direction = (0,-1,-2e-16)
  Length = 40
  Length2 = 10
  Midplane = true
  Profile = -> Sketch002
  ReferenceAxis = -> Sketch002 [N_Axis]
  Type = 0
  expr: Length = Sketch.Constraints.Height
FEATURE [Sketcher::SketchObject] Sketch003
  AttachmentOffset = pos=(0,3,0) rot=(0,0,1;0rad)
  FullyConstrained = true
  MapMode = 5
  Placement = pos=(-7e-16,7e-16,3) rot=(0.57735,0.57735,0.57735;2.0944rad)
  Support = -> [YZ_Plane001]
  expr: .AttachmentOffset.Base.y = <<Pad>>.Length
  expr: Constraints[27] = Sketch.Constraints.Height
  sketch-geometry (21):
    g0: LineSegment StartX=-18 StartY=40 StartZ=0 EndX=-18 EndY=2.5 EndZ=0
    g1: LineSegment StartX=-15.5 StartY=0 StartZ=0 EndX=-3.5 EndY=0 EndZ=0
    g2: LineSegment StartX=-1 StartY=2.5 StartZ=0 EndX=-1 EndY=40 EndZ=0
    g3: LineSegment StartX=-1 StartY=40 StartZ=0 EndX=-18 EndY=40 EndZ=0
    g4: GeomPoint X=-9.5 Y=20 Z=0
    g5: LineSegment StartX=18 StartY=40 StartZ=0 EndX=18 EndY=2.5 EndZ=0
    g6: LineSegment StartX=15.5 StartY=0 StartZ=0 EndX=3.5 EndY=0 EndZ=0
    g7: LineSegment StartX=1 StartY=2.5 StartZ=0 EndX=1 EndY=40 EndZ=0
    g8: LineSegment StartX=1 StartY=40 StartZ=0 EndX=18 EndY=40 EndZ=0
    g9: GeomPoint X=9.5 Y=20 Z=0
    g10: LineSegment StartX=-18 StartY=0 StartZ=0 EndX=-20 EndY=0 EndZ=0
    g11: LineSegment StartX=18 StartY=0 StartZ=0 EndX=20 EndY=0 EndZ=0
    g12: LineSegment StartX=-1 StartY=0 StartZ=0 EndX=1 EndY=0 EndZ=0
    g13: ArcOfCircle CenterX=15.5 CenterY=2.5 CenterZ=0 NormalX=0 NormalY=0 NormalZ=1 AngleXU=0 Radius=2.5 StartAngle=4.71239 EndAngle=6.28319
    g14: GeomPoint X=18 Y=0 Z=0
    g15: ArcOfCircle CenterX=3.5 CenterY=2.5 CenterZ=0 NormalX=0 NormalY=0 NormalZ=1 AngleXU=0 Radius=2.5 StartAngle=3.14159 EndAngle=4.71239
    g16: GeomPoint X=1 Y=0 Z=0
    g17: ArcOfCircle CenterX=-3.5 CenterY=2.5 CenterZ=0 NormalX=0 NormalY=0 NormalZ=1 AngleXU=0 Radius=2.5 StartAngle=4.71239 EndAngle=6.28319
    g18: GeomPoint X=-1 Y=0 Z=0
    g19: ArcOfCircle CenterX=-15.5 CenterY=2.5 CenterZ=0 NormalX=0 NormalY=0 NormalZ=1 AngleXU=0 Radius=2.5 StartAngle=3.14159 EndAngle=4.71239
    g20: GeomPoint X=-18 Y=0 Z=0
  constraints (49):
    c: Coincident(g2,g3)
    c: Coincident(g3,g0)
    c: Horizontal(g1)
    c: Horizontal(g3)
    c: Vertical(g0)
    c: Vertical(g2)
    c: Symmetric(g18,g0,g4)
    c: PointOnObject(g18,g-1)
    c: DistanceY(g18,g2) = 40
    c: Coincident(g7,g8)
    c: Coincident(g8,g5)
    c: Horizontal(g6)
    c: Horizontal(g8)
    c: Vertical(g5)
    c: Vertical(g7)
    c: Symmetric(g16,g5,g9)
    c: Equal(g8,g3)
    c: Symmetric(g18,g16,g-1)
    c: Coincident(g10,g20)
    c: PointOnObject(g10,g-1)
    c: Coincident(g11,g14)
    c: PointOnObject(g11,g-1)
    c: Equal(g11,g10)
    c: Coincident(g12,g18)
    c: Coincident(g12,g16)
    c: Equal(g11,g12)
    c: DistanceX(g11,g11) = 2
    c: DistanceX(g10,g11) = 40
    c: PointOnObject(g14,g5)
    c: PointOnObject(g14,g6)
    c: Tangent(g5,g13) = 1.5708
    c: Tangent(g6,g13) = 1.5708
    c: PointOnObject(g16,g6)
    c: PointOnObject(g16,g7)
    c: Tangent(g6,g15) = 1.5708
    c: Tangent(g7,g15) = 1.5708
    c: Equal(g13,g15)
    c: PointOnObject(g18,g2)
    c: PointOnObject(g18,g1)
    c: Tangent(g2,g17) = -1.5708
    c: Tangent(g1,g17) = -1.5708
    c: PointOnObject(g20,g1)
    c: PointOnObject(g20,g0)
    c: Tangent(g1,g19) = -1.5708
    c: Tangent(g0,g19) = -1.5708
    c: Equal(g17,g19)
    c: Equal(g19,g15)
    c: Radius(g13) = 2.5
    c: PointOnObject(g2,g8)
FEATURE [Part::FeaturePython] Screw  label="M5x16-Screw"  # Fasteners workbench fastener (typed FeaturePython)
  Placement = pos=(0,10,3.5) rot=(0,0,1;0rad)
  baseObject = -> Sketch001 [Edge1]
  diameter = 5
  invert = false
  leftHanded = false
  length = 3
  lengthCustom = 16
  matchOuter = false
  offset = -0.5
  thread = false
  type = 18
FEATURE [Part::FeaturePython] Array_Screw  label="Array_M5x16-Screw"  # Draft array (typed FeaturePython)
  ArraySteps = 0
  ArrayType = Circular Array
  Axis = LCS_Origin.Z
  Count = 2
  ElementCount = 2
  FullAngle = 360
  IntervalAngle = 180
  LinearSteps = 0
  PlacementList = 2 placements: [(0,10,3.5),(-1.22465e-15,-10,3.5)]
  ScaleList = (2) [(1,1,1),(1,1,1)]
  ShowElement = false
  SourceObject = -> Screw
FEATURE [App::DocumentObjectGroup] Fasteners
  Group = -> [Screw,Array_Screw]
FEATURE [PartDesign::Mirrored] Mirrored  label="RibMirror"
  BaseFeature = -> Pad001
  MirrorPlane = -> Sketch002 [V_Axis]
  Originals = -> [Pad001]
FEATURE [PartDesign::Pocket] Pocket  label="RibGap"
  BaseFeature = -> Mirrored
  Direction = (-1,2e-16,-3e-16)
  Length = 5
  Length2 = 5
  Midplane = true
  Profile = -> Sketch003
  ReferenceAxis = -> Sketch003 [N_Axis]
  Type = 1
FEATURE [Sketcher::SketchObject] Sketch004
  FullyConstrained = true
  MapMode = 5
  Support = -> [XY_Plane001]
  sketch-geometry (15):
    g0: ArcOfCircle CenterX=-19 CenterY=17 CenterZ=0 NormalX=0 NormalY=0 NormalZ=1 AngleXU=0 Radius=3 StartAngle=1.5708 EndAngle=3.14159
    g1: LineSegment StartX=-19 StartY=20 StartZ=0 EndX=19 EndY=20 EndZ=0
    g2: ArcOfCircle CenterX=19 CenterY=17 CenterZ=0 NormalX=0 NormalY=0 NormalZ=1 AngleXU=0 Radius=3 StartAngle=3e-16 EndAngle=1.5708
    g3: LineSegment StartX=22 StartY=17 StartZ=0 EndX=22 EndY=-17 EndZ=0
    g4: ArcOfCircle CenterX=19 CenterY=-17 CenterZ=0 NormalX=0 NormalY=0 NormalZ=1 AngleXU=0 Radius=3 StartAngle=4.71239 EndAngle=6.28319
    g5: LineSegment StartX=19 StartY=-20 StartZ=0 EndX=-19 EndY=-20 EndZ=0
    g6: ArcOfCircle CenterX=-19 CenterY=-17 CenterZ=0 NormalX=0 NormalY=0 NormalZ=1 AngleXU=0 Radius=3 StartAngle=3.14159 EndAngle=4.71239
    g7: LineSegment StartX=-22 StartY=-17 StartZ=0 EndX=-22 EndY=17 EndZ=0
    g8: GeomPoint X=-22 Y=20 Z=0
    g9: GeomPoint X=22 Y=-20 Z=0
    g10: LineSegment StartX=23 StartY=-21 StartZ=0 EndX=23 EndY=21 EndZ=0
    g11: LineSegment StartX=23 StartY=21 StartZ=0 EndX=-23 EndY=21 EndZ=0
    g12: LineSegment StartX=-23 StartY=21 StartZ=0 EndX=-23 EndY=-21 EndZ=0
    g13: LineSegment StartX=-23 StartY=-21 StartZ=0 EndX=23 EndY=-21 EndZ=0
    g14: GeomPoint X=0 Y=0 Z=0
  constraints (35):
    c: Tangent(g0,g1) = 1.5708
    c: Tangent(g1,g2) = 1.5708
    c: Tangent(g2,g3) = 1.5708
    c: Tangent(g3,g4) = 1.5708
    c: Tangent(g4,g5) = 1.5708
    c: Tangent(g5,g6) = 1.5708
    c: Tangent(g6,g7) = 1.5708
    c: Tangent(g7,g0) = 1.5708
    c: Horizontal(g1)
    c: Horizontal(g5)
    c: Vertical(g3)
    c: Vertical(g7)
    c: Equal(g0,g2)
    c: Equal(g2,g4)
    c: Equal(g4,g6)
    c: PointOnObject(g8,g1)
    c: PointOnObject(g8,g7)
    c: PointOnObject(g9,g3)
    c: PointOnObject(g9,g5)
    c: Symmetric(g4,g0,g-1)
    c: Radius(g2) = 3
    c: DistanceY(g4,g1) = 40  'Height'
    c: DistanceX(g6,g3) = 44  'Width'
    c: Coincident(g10,g11)
    c: Coincident(g11,g12)
    c: Coincident(g12,g13)
    c: Coincident(g13,g10)
    c: Horizontal(g11)
    c: Horizontal(g13)
    c: Vertical(g10)
    c: Vertical(g12)
    c: Symmetric(g11,g10,g14)
    c: Coincident(g14,g-1)
    c: DistanceY(g0,g11) = 1
    c: DistanceX(g12,g6) = 1
FEATURE [PartDesign::Pocket] Pocket001  label="CornerFillets"
  BaseFeature = -> Pocket
  Direction = (0,0,-1)
  Length = 5
  Length2 = 5
  Midplane = true
  Profile = -> Sketch004
  ReferenceAxis = -> Sketch004 [N_Axis]
  Type = 1
FEATURE [PartDesign::Hole] Hole  label="MountHoles"
  BaseFeature = -> Pocket001
  CustomThreadClearance = 0
  Depth = 25
  DepthType = 0
  Diameter = 5.5
  DrillForDepth = false
  DrillPoint = 1
  DrillPointAngle = 118
  HoleCutCountersinkAngle = 90
  HoleCutCustomValues = false
  HoleCutDepth = 0
  HoleCutDiameter = 12.2
  HoleCutType = 7
  ModelThread = false
  Profile = -> Sketch001
  Tapered = false
  TaperedAngle = 90
  ThreadClass = 0
  ThreadDepth = 25
  ThreadDepthType = 0
  ThreadDirection = 0
  ThreadFit = 0
  ThreadSize = 13
  ThreadType = 1
  Threaded = false
  UseCustomThreadClearance = false
FEATURE [PartDesign::Body] Body
  Group = -> [Sketch,Pad,Sketch001,Sketch002,Pad001,Sketch003,Mirrored,Pocket,Sketch004,Pocket001,Hole]
  Origin = -> Origin001
  Tip = -> Hole
FEATURE [App::Part] Assembly
  AssemblyType = Part::Link
  Group = -> [LCS_Origin,Variables,Constraints,Configurations,Body,Fasteners,Screw,Array_Screw]
  Origin = -> Origin
  Type = Assembly
---- part Params.FCStd = doc fcstd_b8f81ed59c9d ----
FCSTD DOCUMENT  (FreeCAD 0.20R29177 +426 (Git))
Label: Params
License: All rights reserved
LicenseURL: http://en.wikipedia.org/wiki/All_rights_reserved
objects: Spreadsheet::Sheet×1

FEATURE [Spreadsheet::Sheet] Spreadsheet  label="Params"
  cells = A1=DriveWheelWidth; B1(DriveWheelWidth)=10; D1=PlywoodThickness; E1(PlywoodThickness)=18.5; A2=DriveWheelMajorDiameter; B2(DriveWheelMajorDiameter)=52; D2=ExtensionArmCenterOffset; E2(ExtensionArmCenterOffset)=23; A3=DriveWheelCrown; B3(DriveWheelCrown)=2; D3=SheetMetalThickness; E3(SheetMetalThickness)=2.656; A4=DriveWheelTireThickness; B4(DriveWheelTireThickness)=3; D4=CeilingPlateDiameter; E4(CeilingPlateDiameter)=463; A6=DriveUnitAngle; B6(DriveUnitAngle)=30; D6=TableRollerMountHoleSpacing; E6(TableRollerMountHoleSpacing)=24; A7=DriveRadius; B7(DriveRadius)=280; D7=TableRollerMountHoleOffset; E7(TableRollerMountHoleOffset)=12; A8=DriveAdjMiddleOffset; B8(DriveAdjMiddleOffset)=90; D8=TableRollerDriveSupportRadius; E8(TableRollerDriveSupportRadius)=218; A9=RotationDriveOffset; B9(RotationDriveOffset)=29; D9=TableRollerSideRadius; E9(TableRollerSideRadius)=164; A10=FrontSkateOffset; B10(FrontSkateOffset)=350; D10=TableRollerDriveSupportAngle; E10(TableRollerDriveSupportAngle)=13.5; A11=RearSkateOffset; B11(RearSkateOffset)=150; D11=TableRollerSideAngle; E11(TableRollerSideAngle)=20; A13=CablePulleyDiameter; B13(CablePulleyDiameter)=120; D13=RoomWidth; E13(RoomWidth)=3650; D14=RoomLength; E14(RoomLength)=3650; A15=ExtensionDriverOffsetX; B15(ExtensionDriverOffsetX)=100; D15=RoomHeight; E15(RoomHeight)=2440; A16=ExtensionDriverOffsetY; B16(ExtensionDriverOffsetY)=-36
